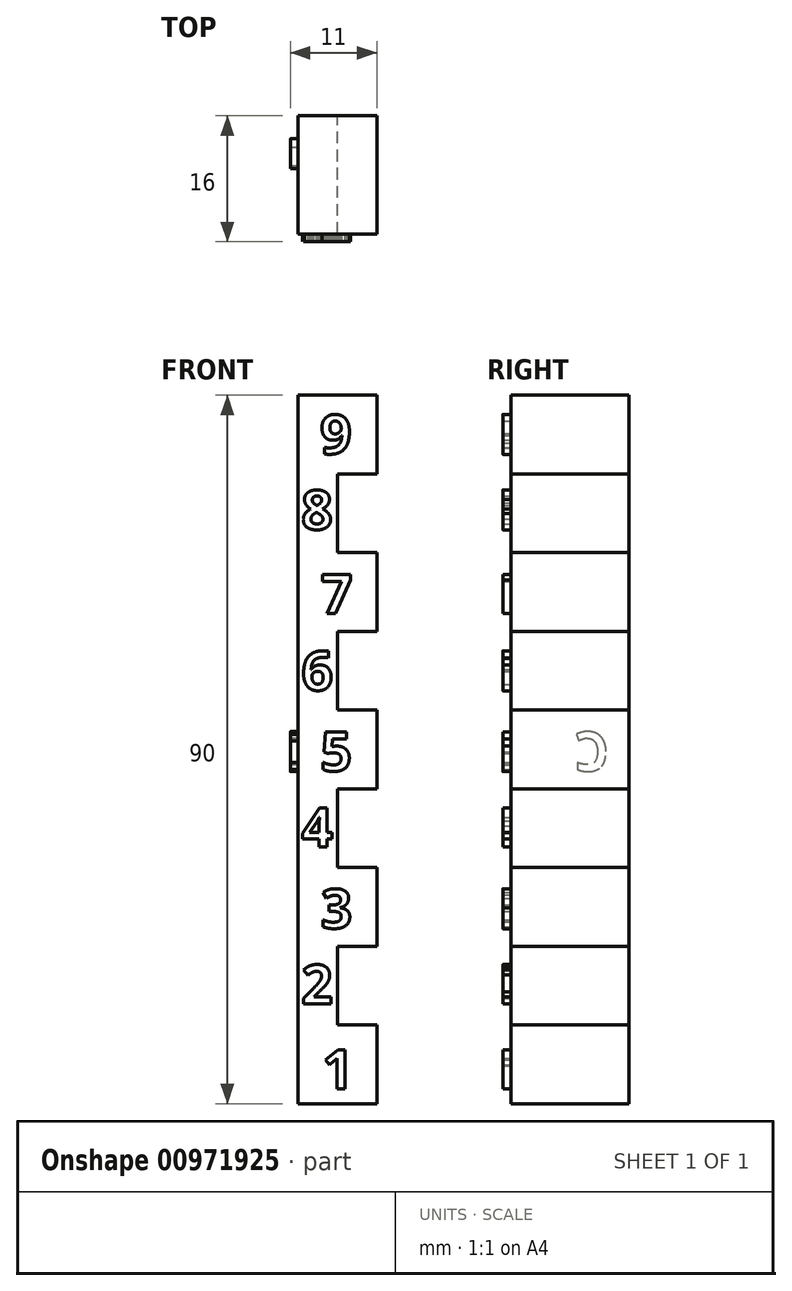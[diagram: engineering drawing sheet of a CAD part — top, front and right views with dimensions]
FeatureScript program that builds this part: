
annotation { "Feature Type Name" : "Feature", "Feature Type Description" : "" }
export const myFeature = defineFeature(function(context is Context, id is Id, definition is map)
    precondition{}
    {
        {
            var Q0;
            Q0=qCreatedBy(makeId("Front.planeOp"),FACE);
            var sketch = newSketch(context, id + "F0", { "sketchPlane" : qUnion([Q0])});
            skLineSegment(sketch, "E0.bottom", {"start": v(17.7, -36.3) * mm, "end": v(22.7, -36.3) * mm});
            skLineSegment(sketch, "E0.left", {"start": v(17.7, -36.3) * mm, "end": v(17.7, 53.7) * mm});
            skLineSegment(sketch, "E0.right", {"start": v(22.7, -26.3) * mm, "end": v(22.7, -16.3) * mm});
            skLineSegment(sketch, "E1", {"start": v(22.7, -36.3) * mm, "end": v(27.7, -36.3) * mm});
            skLineSegment(sketch, "E2", {"start": v(27.7, -36.3) * mm, "end": v(27.7, -26.3) * mm});
            skLineSegment(sketch, "E3", {"start": v(27.7, -26.3) * mm, "end": v(22.7, -26.3) * mm});
            skLineSegment(sketch, "E4", {"start": v(22.7, -16.3) * mm, "end": v(27.7, -16.3) * mm});
            skLineSegment(sketch, "E5", {"start": v(27.7, -16.3) * mm, "end": v(27.7, -6.3) * mm});
            skLineSegment(sketch, "E6", {"start": v(27.7, -6.3) * mm, "end": v(22.7, -6.3) * mm});
            skLineSegment(sketch, "E7", {"start": v(22.7, 3.7) * mm, "end": v(27.7, 3.7) * mm});
            skLineSegment(sketch, "E8", {"start": v(27.7, 3.7) * mm, "end": v(27.7, 13.7) * mm});
            skLineSegment(sketch, "E9", {"start": v(27.7, 13.7) * mm, "end": v(22.7, 13.7) * mm});
            skLineSegment(sketch, "E10", {"start": v(22.7, 23.7) * mm, "end": v(27.7, 23.7) * mm});
            skLineSegment(sketch, "E11", {"start": v(27.7, 23.7) * mm, "end": v(27.7, 33.7) * mm});
            skLineSegment(sketch, "E12", {"start": v(27.7, 33.7) * mm, "end": v(22.7, 33.7) * mm});
            skLineSegment(sketch, "E13", {"start": v(22.7, 43.7) * mm, "end": v(27.7, 43.7) * mm});
            skLineSegment(sketch, "E14", {"start": v(27.7, 43.7) * mm, "end": v(27.7, 53.7) * mm});
            skLineSegment(sketch, "E15.trimOffspring", {"start": v(22.7, 33.7) * mm, "end": v(22.7, 43.7) * mm});
            skLineSegment(sketch, "E16.trimOffspring", {"start": v(22.7, 13.7) * mm, "end": v(22.7, 23.7) * mm});
            skLineSegment(sketch, "E17.trimOffspring", {"start": v(22.7, -6.3) * mm, "end": v(22.7, 3.7) * mm});
            skLineSegment(sketch, "E18", {"start": v(17.7, 53.7) * mm, "end": v(27.7, 53.7) * mm});
            skSolve(sketch);
        }
        {
            var Q0;
            Q0=makeQuery(id+"F0.imprint","IMPRINT",FACE,{"disambiguationData":[TD([[makeQuery(id+"F0.imprint","IMPRINT",EDGE,{"derivedFrom":sQuery(id+"F0.wireOp",EDGE,"E0.bottom")}),1.0]])]});
            extrude(context, id + "F1", {"entities" : qUnion([Q0]), "depth" : 15 * mm, "offsetDistance" : 25 * mm});
        }
        {
            var Q0;
            Q0=makeQuery(id+"F1.opExtrude","CAP_FACE",FACE,{"disambiguationData":[OSD([sQuery(id+"F0.wireOp",EDGE,"E0.bottom"),sQuery(id+"F0.wireOp",EDGE,"E0.top"),sQuery(id+"F0.wireOp",EDGE,"E0.left"),sQuery(id+"F0.wireOp",EDGE,"E0.right"),sQuery(id+"F0.wireOp",EDGE,"E1"),sQuery(id+"F0.wireOp",EDGE,"E2"),sQuery(id+"F0.wireOp",EDGE,"E3"),sQuery(id+"F0.wireOp",EDGE,"E4"),sQuery(id+"F0.wireOp",EDGE,"E5"),sQuery(id+"F0.wireOp",EDGE,"E6"),sQuery(id+"F0.wireOp",EDGE,"E7"),sQuery(id+"F0.wireOp",EDGE,"E8"),sQuery(id+"F0.wireOp",EDGE,"E9"),sQuery(id+"F0.wireOp",EDGE,"E10"),sQuery(id+"F0.wireOp",EDGE,"E11"),sQuery(id+"F0.wireOp",EDGE,"E12"),sQuery(id+"F0.wireOp",EDGE,"E13"),sQuery(id+"F0.wireOp",EDGE,"E14"),sQuery(id+"F0.wireOp",EDGE,"GW2VGPY7-JH1h-TVn8-Ep0i-d1FX4UWYeuMp"),sQuery(id+"F0.wireOp",EDGE,"9GAQt9xi-YV9q-x5FU-JGIx-CzgDCV1lQXgC"),sQuery(id+"F0.wireOp",EDGE,"6qqABKLI-dhLt-BX4q-IHTr-V4MQ4PMBYTkY"),sQuery(id+"F0.wireOp",EDGE,"EeBTtjjH-9KYH-6P8U-PVpf-X93rzg4klSRn"),sQuery(id+"F0.wireOp",EDGE,"SQ0iFLqb-gNZB-jgxF-iGu9-uG40gg3OiHo4"),sQuery(id+"F0.wireOp",EDGE,"gWCKqSfi-57VO-fZMF-MSuw-Q9kWZPC2wlJe"),sQuery(id+"F0.wireOp",EDGE,"tKBunrKC-Zp2K-BgY0-Ykj0-yCIUoT3ddA2M"),sQuery(id+"F0.wireOp",EDGE,"Qz7bPEcf-0afa-G3GZ-vYAb-HkHly8ZGF2Jc"),sQuery(id+"F0.wireOp",EDGE,"8oUR93dQ-nMIL-AeUH-uZ8D-f2vf18d7PPYC"),sQuery(id+"F0.wireOp",EDGE,"t9m2MhqW-Fsgu-5oEN-ydM3-bzSSf0wwiARf"),sQuery(id+"F0.wireOp",EDGE,"9af4eb42-e277-40ed-bdf6-f4ce172837da.trimOffspring"),sQuery(id+"F0.wireOp",EDGE,"fa716bd0-a6ce-4781-b928-c7b11fe5377b.trimOffspring"),sQuery(id+"F0.wireOp",EDGE,"3aa8a900-0061-4581-880f-1083a1359717.trimOffspring"),sQuery(id+"F0.wireOp",EDGE,"E15.trimOffspring"),sQuery(id+"F0.wireOp",EDGE,"E16.trimOffspring"),sQuery(id+"F0.wireOp",EDGE,"E17.trimOffspring")])],"isStart":false});
            var sketch = newSketch(context, id + "F2", { "sketchPlane" : qUnion([Q0])});
            skText(sketch, "E19", { "text": "1", "fontName": "OpenSans-Bold.ttf"});
            skText(sketch, "E20", { "text": "2", "fontName": "OpenSans-Bold.ttf"});
            skText(sketch, "E21", { "text": "3", "fontName": "OpenSans-Bold.ttf"});
            skText(sketch, "E22", { "text": "4", "fontName": "OpenSans-Bold.ttf"});
            skText(sketch, "E23", { "text": "5", "fontName": "OpenSans-Bold.ttf"});
            skText(sketch, "E24", { "text": "6", "fontName": "OpenSans-Bold.ttf"});
            skText(sketch, "E25", { "text": "7", "fontName": "OpenSans-Bold.ttf"});
            skText(sketch, "E26", { "text": "8", "fontName": "OpenSans-Bold.ttf"});
            skText(sketch, "E27", { "text": "9", "fontName": "OpenSans-Bold.ttf"});
            const initialGuessF2  = {"E19": [0.02078, -0.0344, 1, 0, 0.005], "E20": [0.0181, -0.02365, 1, 0, 0.005], "E21": [0.02056, -0.01402, 1, 0, 0.005], "E22": [0.01812, -0.00372, 1, 0, 0.005], "E23": [0.02054, 0.00595, 1, 0, 0.005], "E24": [0.01814, 0.01621, 1, 0, 0.005], "E25": [0.0206, 0.02595, 1, 0, 0.005], "E26": [0.0181, 0.03664, 1, 0, 0.005], "E27": [0.02049, 0.04625, 1, 0, 0.005]};
            skSetInitialGuess(sketch, initialGuessF2);
            skSolve(sketch);
        }
        {
            var Q0;
            Q0=qSketchRegion(id+"F2",true);
            extrude(context, id + "F3", {"entities" : qUnion([Q0]), "operationType" : NewBodyOperationType.ADD, "depth" : 1 * mm, "offsetDistance" : 25 * mm});
        }
        {
            var Q0;
            Q0=makeQuery(id+"F1.opExtrude","SWEPT_FACE",FACE,{"disambiguationData":[OSD([sQuery(id+"F0.wireOp",EDGE,"E0.left")])]});
            var sketch = newSketch(context, id + "F4", { "sketchPlane" : qUnion([Q0])});
            skText(sketch, "E28", { "text": "C", "fontName": "OpenSans-Bold.ttf"});
            const initialGuessF4  = {"E28": [0.0025, 0.00595, 1, 0, 0.005]};
            skSetInitialGuess(sketch, initialGuessF4);
            skSolve(sketch);
        }
        {
            var Q0;
            Q0 = qSketchRegion(id + "F4", true);
            extrude(context, id + "F5", {"entities" : qUnion([Q0]), "operationType" : NewBodyOperationType.ADD, "depth" : 1 * mm, "offsetDistance" : 25 * mm});
        }
    });
